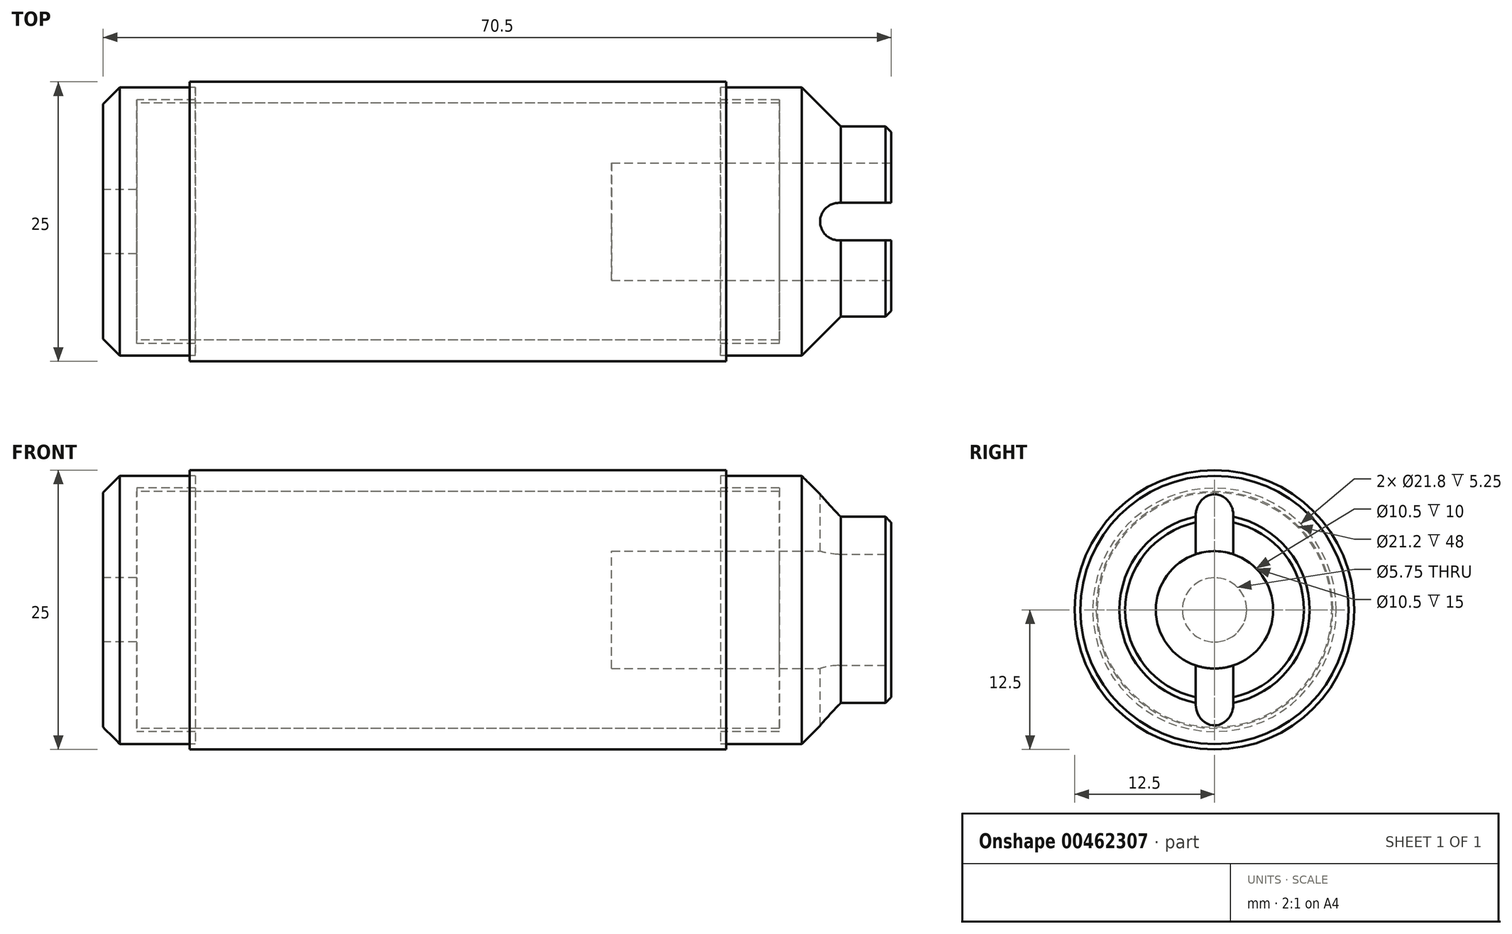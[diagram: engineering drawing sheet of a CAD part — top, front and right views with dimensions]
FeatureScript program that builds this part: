
annotation { "Feature Type Name" : "Feature", "Feature Type Description" : "" }
export const myFeature = defineFeature(function(context is Context, id is Id, definition is map)
    precondition{}
    {
        {
            var Q0;
            Q0=qCreatedBy(makeId("Right.planeOp"),FACE);
            var sketch = newSketch(context, id + "F0", { "sketchPlane" : qUnion([Q0])});
            skCircle(sketch, "E0", {"center": v(0, 0) * mm, "radius": 10.6 * mm});
            skSolve(sketch);
        }
        {
            var Q0;
            Q0 = qSketchRegion(id + "F0", true);
            extrude(context, id + "F1", {"entities" : qUnion([Q0]), "endBound" : BoundingType.SYMMETRIC, "depth" : 57.5 * mm});
        }
        {
            var Q0;
            Q0=qCreatedBy(makeId("Right.planeOp"),FACE);
            var sketch = newSketch(context, id + "F2", { "sketchPlane" : qUnion([Q0])});
            skCircle(sketch, "E1.0", {"center": v(0, 0) * mm, "radius": 10.6 * mm});
            skCircle(sketch, "E2", {"center": v(0, 0) * mm, "radius": 12.5 * mm});
            skSolve(sketch);
        }
        {
            var Q0;
            Q0 = qSketchRegion(id + "F2", true);
            extrude(context, id + "F3", {"entities" : qUnion([Q0]), "endBound" : BoundingType.SYMMETRIC, "depth" : 48 * mm});
        }
        {
            var Q0;
            Q0=qCreatedBy(makeId("Front.planeOp"),FACE);
            var sketch = newSketch(context, id + "F4", { "sketchPlane" : qUnion([Q0])});
            skLineSegment(sketch, "E3", {"start": v(23.5, 12) * mm, "end": v(23.5, 10.9) * mm});
            skLineSegment(sketch, "E4", {"start": v(23.5, 10.9) * mm, "end": v(28.75, 10.9) * mm});
            skLineSegment(sketch, "E5", {"start": v(28.75, 10.9) * mm, "end": v(28.75, 0) * mm});
            skLineSegment(sketch, "E6", {"start": v(28.75, 0) * mm, "end": v(38.75, 0) * mm});
            skLineSegment(sketch, "E7", {"start": v(38.75, 0) * mm, "end": v(38.75, 8.5) * mm});
            skLineSegment(sketch, "E8", {"start": v(38.75, 8.5) * mm, "end": v(34.25, 8.5) * mm});
            skLineSegment(sketch, "E9", {"start": v(34.25, 8.5) * mm, "end": v(30.75, 12) * mm});
            skLineSegment(sketch, "E10", {"start": v(30.75, 12) * mm, "end": v(23.5, 12) * mm});
            skPoint(sketch, "E11", {"position": v(28.75, 10.6) * mm});
            skLineSegment(sketch, "E12", {"start": v(-23.5, 12) * mm, "end": v(-31.75, 12) * mm});
            skLineSegment(sketch, "E13", {"start": v(-31.75, 12) * mm, "end": v(-31.75, 4) * mm});
            skLineSegment(sketch, "E14", {"start": v(-28.75, 2.87) * mm, "end": v(-32.75, 2.87) * mm});
            skLineSegment(sketch, "E15", {"start": v(-28.75, 2.87) * mm, "end": v(-28.75, 10.9) * mm});
            skLineSegment(sketch, "E16", {"start": v(-28.75, 10.9) * mm, "end": v(-23.5, 10.9) * mm});
            skLineSegment(sketch, "E17", {"start": v(-23.5, 10.9) * mm, "end": v(-23.5, 12) * mm});
            skLineSegment(sketch, "E18", {"start": v(-32.75, 2.87) * mm, "end": v(-32.75, 4) * mm});
            skLineSegment(sketch, "E19", {"start": v(-32.75, 4) * mm, "end": v(-31.75, 4) * mm});
            skLineSegment(sketch, "E20", {"start": v(-38.75, 0) * mm, "end": v(38.75, 0) * mm, "construction": true});
            skSolve(sketch);
        }
        {
            var Q0;
            Q0 = qSketchRegion(id + "F4", true);
            var Q1;
            Q1=sQuery(id+"F4.wireOp",EDGE,"E20");
            revolve(context, id + "F5", {"entities" : qUnion([Q0]), "axis" : qUnion([Q1]), "revolveType" : RevolveType.FULL});
        }
        {
            var Q0;
            Q0=makeQuery(id+"F5.opRevolve","SWEPT_EDGE",EDGE,{"disambiguationData":[OSD([sQuery(id+"F4.wireOp",EDGE,"E12"),sQuery(id+"F4.wireOp",EDGE,"E13")])]});
            chamfer(context, id + "F6", {"entities" : qUnion([Q0]), "width" : 1.5 * mm, "tangentPropagation" : true});
        }
        {
            var Q0;
            Q0=makeQuery(id+"F5.opRevolve","SWEPT_FACE",FACE,{"disambiguationData":[OSD([sQuery(id+"F4.wireOp",EDGE,"E18")])]});
            var sketch = newSketch(context, id + "F7", { "sketchPlane" : qUnion([Q0])});
            skCircle(sketch, "E21.0", {"center": v(0, 0) * mm, "radius": 4 * mm});
            skSolve(sketch);
        }
        {
            var Q0;
            Q0 = qSketchRegion(id + "F7", true);
            var Q1;
            Q1=makeQuery(id+"F5.opRevolve","SWEPT_FACE",FACE,{"disambiguationData":[OSD([sQuery(id+"F4.wireOp",EDGE,"E13")])]});
            extrude(context, id + "F8", {"entities" : qUnion([Q0]), "operationType" : NewBodyOperationType.REMOVE, "endBound" : BoundingType.UP_TO_SURFACE, "oppositeDirection" : true, "endBoundEntityFace" : qUnion([Q1]), "depth" : 25 * mm});
        }
        {
            var Q0;
            Q0=makeQuery(id+"F5.opRevolve","SWEPT_FACE",FACE,{"disambiguationData":[OSD([sQuery(id+"F4.wireOp",EDGE,"E7")])]});
            var sketch = newSketch(context, id + "F9", { "sketchPlane" : qUnion([Q0])});
            skCircle(sketch, "E22", {"center": v(0, 0) * mm, "radius": 5.25 * mm});
            skSolve(sketch);
        }
        {
            var Q0;
            Q0 = qSketchRegion(id + "F9", true);
            extrude(context, id + "F10", {"entities" : qUnion([Q0]), "operationType" : NewBodyOperationType.REMOVE, "oppositeDirection" : true, "depth" : 25 * mm, "offsetDistance" : 25 * mm});
        }
        {
            var Q0;
            Q0=qCreatedBy(makeId("Top.planeOp"),FACE);
            var sketch = newSketch(context, id + "F11", { "sketchPlane" : qUnion([Q0])});
            skArc(sketch, "E23", {"start": v(34.07, 1.68) * mm, "mid": v(32.4, 0) * mm, "end": v(34.07, -1.68) * mm});
            skLineSegment(sketch, "E24.bottom", {"start": v(34.07, -1.68) * mm, "end": v(38.75, -1.68) * mm});
            skLineSegment(sketch, "E24.top", {"start": v(34.07, 1.68) * mm, "end": v(38.75, 1.68) * mm});
            skLineSegment(sketch, "E24.left", {"start": v(34.07, -1.67) * mm, "end": v(34.07, 1.67) * mm, "construction": true});
            skLineSegment(sketch, "E24.right", {"start": v(38.75, -1.68) * mm, "end": v(38.75, 1.68) * mm});
            skSolve(sketch);
        }
        {
            var Q0;
            Q0 = qSketchRegion(id + "F11", true);
            extrude(context, id + "F12", {"entities" : qUnion([Q0]), "operationType" : NewBodyOperationType.REMOVE, "endBound" : BoundingType.THROUGH_ALL, "oppositeDirection" : true, "depth" : 25 * mm, "offsetDistance" : 25 * mm, "hasSecondDirection" : true, "secondDirectionBound" : SecondDirectionBoundingType.THROUGH_ALL, "secondDirectionOppositeDirection" : false, "secondDirectionDepth" : 25 * mm});
        }
        {
            var Q0;
            {var subQ0=sQuery(id+"F4.wireOp",EDGE,"E7");var subQ1=sQuery(id+"F4.wireOp",EDGE,"E8");Q0=makeQuery(id+"F12.boolean.opBoolean","SPLIT",EDGE,{"disambiguationData":[TD([makeQuery(id+"F12.opExtrude","SWEPT_FACE",FACE,{"disambiguationData":[OSD([sQuery(id+"F11.wireOp",EDGE,"E24.top")])]})])],"derivedFrom":makeQuery(id+"F5.opRevolve","SWEPT_EDGE",EDGE,{"disambiguationData":[OSD([subQ0,subQ1])]})});}
            var Q1;
            {var subQ0=sQuery(id+"F4.wireOp",EDGE,"E7");var subQ1=sQuery(id+"F4.wireOp",EDGE,"E8");Q1=makeQuery(id+"F12.boolean.opBoolean","SPLIT",EDGE,{"disambiguationData":[TD([makeQuery(id+"F12.opExtrude","SWEPT_FACE",FACE,{"disambiguationData":[OSD([sQuery(id+"F11.wireOp",EDGE,"E24.bottom")])]})])],"derivedFrom":makeQuery(id+"F5.opRevolve","SWEPT_EDGE",EDGE,{"disambiguationData":[OSD([subQ0,subQ1])]})});}
            var Q2;
            {var subQ0=sQuery(id+"F9.wireOp",EDGE,"E22");Q2=makeQuery(id+"F12.boolean.opBoolean","SPLIT",EDGE,{"disambiguationData":[TD([makeQuery(id+"F12.opExtrude","SWEPT_FACE",FACE,{"disambiguationData":[OSD([sQuery(id+"F11.wireOp",EDGE,"E24.bottom")])]})])],"derivedFrom":makeQuery(id+"F10.boolean.opBoolean","COPY",EDGE,{"derivedFrom":makeQuery(id+"F10.opExtrude","CAP_EDGE",EDGE,{"disambiguationData":[OSD([subQ0])],"isStart":true})})});}
            var Q3;
            {var subQ0=sQuery(id+"F9.wireOp",EDGE,"E22");Q3=makeQuery(id+"F12.boolean.opBoolean","SPLIT",EDGE,{"disambiguationData":[TD([makeQuery(id+"F12.opExtrude","SWEPT_FACE",FACE,{"disambiguationData":[OSD([sQuery(id+"F11.wireOp",EDGE,"E24.top")])]})])],"derivedFrom":makeQuery(id+"F10.boolean.opBoolean","COPY",EDGE,{"derivedFrom":makeQuery(id+"F10.opExtrude","CAP_EDGE",EDGE,{"disambiguationData":[OSD([subQ0])],"isStart":true})})});}
            chamfer(context, id + "F13", {"entities" : qUnion([Q0, Q1, Q2, Q3]), "width" : .5 * mm, "tangentPropagation" : true});
        }
    });
